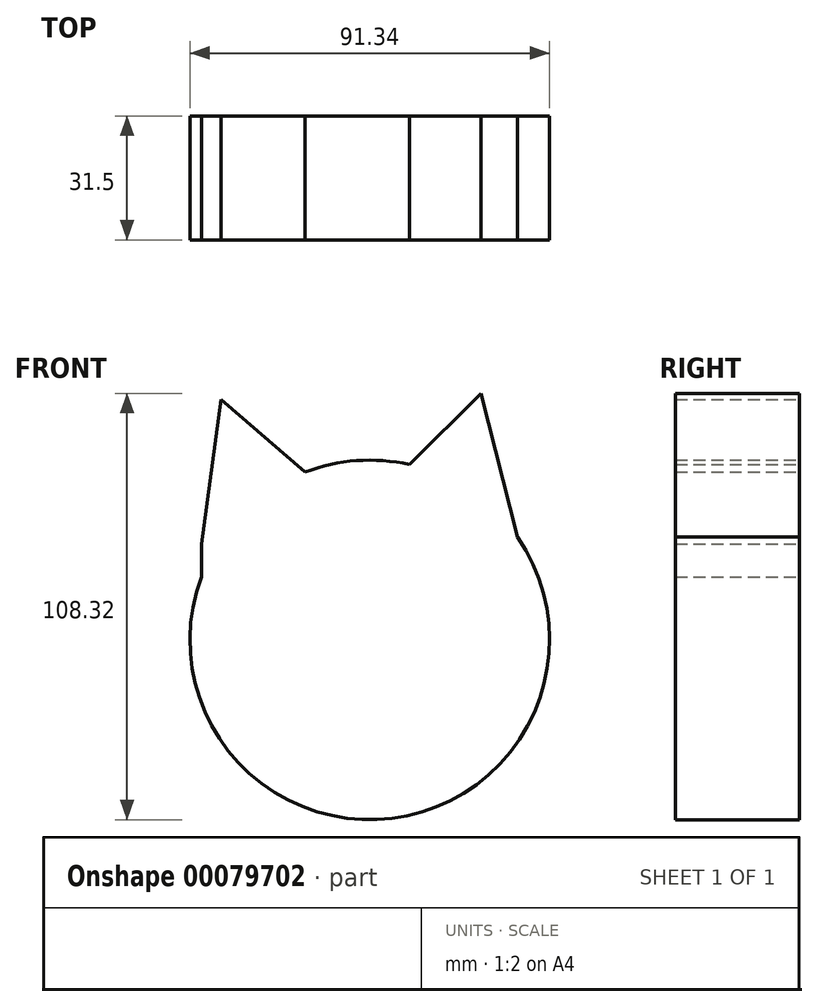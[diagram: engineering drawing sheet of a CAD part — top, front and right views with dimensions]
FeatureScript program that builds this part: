
annotation { "Feature Type Name" : "Feature", "Feature Type Description" : "" }
export const myFeature = defineFeature(function(context is Context, id is Id, definition is map)
    precondition{}
    {
        {
            var Q0;
            Q0=qCreatedBy(makeId("Front.planeOp"),FACE);
            var sketch = newSketch(context, id + "F0", { "sketchPlane" : qUnion([Q0])});
            skCircle(sketch, "E0", {"center": v(0, 0) * mm, "radius": 45.67 * mm});
            skLineSegment(sketch, "E1", {"start": v(-42.78, 24.42) * mm, "end": v(-37.81, 61.08) * mm});
            skLineSegment(sketch, "E2", {"start": v(-37.81, 61.08) * mm, "end": v(-16.43, 42.61) * mm});
            skLineSegment(sketch, "E3", {"start": v(-42.78, 24.42) * mm, "end": v(-42.78, 16) * mm});
            skLineSegment(sketch, "E4", {"start": v(10.07, 44.55) * mm, "end": v(28.22, 62.65) * mm});
            skLineSegment(sketch, "E5", {"start": v(28.22, 62.65) * mm, "end": v(37.47, 26.1) * mm});
            skSolve(sketch);
        }
        {
            var Q0;
            {var subQ0=sQuery(id+"F0.wireOp",EDGE,"E0");var subQ1=makeQuery(id+"F0.imprint","INTERSECT",VERTEX,{"derivedFrom":[subQ0,sQuery(id+"F0.wireOp",EDGE,"E4")]});Q0=makeQuery(id+"F0.imprint","IMPRINT",FACE,{"disambiguationData":[TD([[makeQuery(id+"F0.imprint","IMPRINT",EDGE,{"disambiguationData":[TD([[subQ1,1.0]])],"derivedFrom":subQ0}),1.0]])]});}
            var Q1;
            Q1=makeQuery(id+"F0.imprint","IMPRINT",FACE,{"disambiguationData":[TD([[makeQuery(id+"F0.imprint","IMPRINT",EDGE,{"derivedFrom":sQuery(id+"F0.wireOp",EDGE,"E1")}),-1.0]])]});
            var Q2;
            {var subQ0=sQuery(id+"F0.wireOp",EDGE,"E4");Q2=makeQuery(id+"F0.imprint","IMPRINT",FACE,{"disambiguationData":[TD([[makeQuery(id+"F0.imprint","IMPRINT",EDGE,{"derivedFrom":subQ0}),-1.0]])]});}
            extrude(context, id + "F1", {"entities" : qUnion([Q0, Q1, Q2]), "depth" : 25.4 * mm});
        }
        {
            var Q0;
            Q0=qCreatedBy(makeId("Front.planeOp"),FACE);
            var sketch = newSketch(context, id + "F2", { "sketchPlane" : qUnion([Q0])});
            skCircle(sketch, "E6", {"center": v(-20.02, 13.2) * mm, "radius": 9.23 * mm});
            skCircle(sketch, "E7", {"center": v(12.14, 13.2) * mm, "radius": 9.73 * mm});
            skSolve(sketch);
        }
        {
            var Q0;
            Q0=makeQuery(id+"F1.opExtrude","CAP_FACE",FACE,{"disambiguationData":[OSD([sQuery(id+"F0.wireOp",EDGE,"E0"),sQuery(id+"F0.wireOp",EDGE,"E1"),sQuery(id+"F0.wireOp",EDGE,"E2"),sQuery(id+"F0.wireOp",EDGE,"E3"),sQuery(id+"F0.wireOp",EDGE,"E4"),sQuery(id+"F0.wireOp",EDGE,"E5")])],"isStart":false});
            var Q1;
            Q1=makeQuery(id+"F2.imprint","IMPRINT",FACE,{"disambiguationData":[TD([[makeQuery(id+"F2.imprint","IMPRINT",EDGE,{"derivedFrom":sQuery(id+"F2.wireOp",EDGE,"E7")}),1.0]])]});
            extrude(context, id + "F3", {"entities" : qUnion([Q0, Q1]), "operationType" : NewBodyOperationType.ADD, "depth" : 6.1 * mm});
        }
    });
